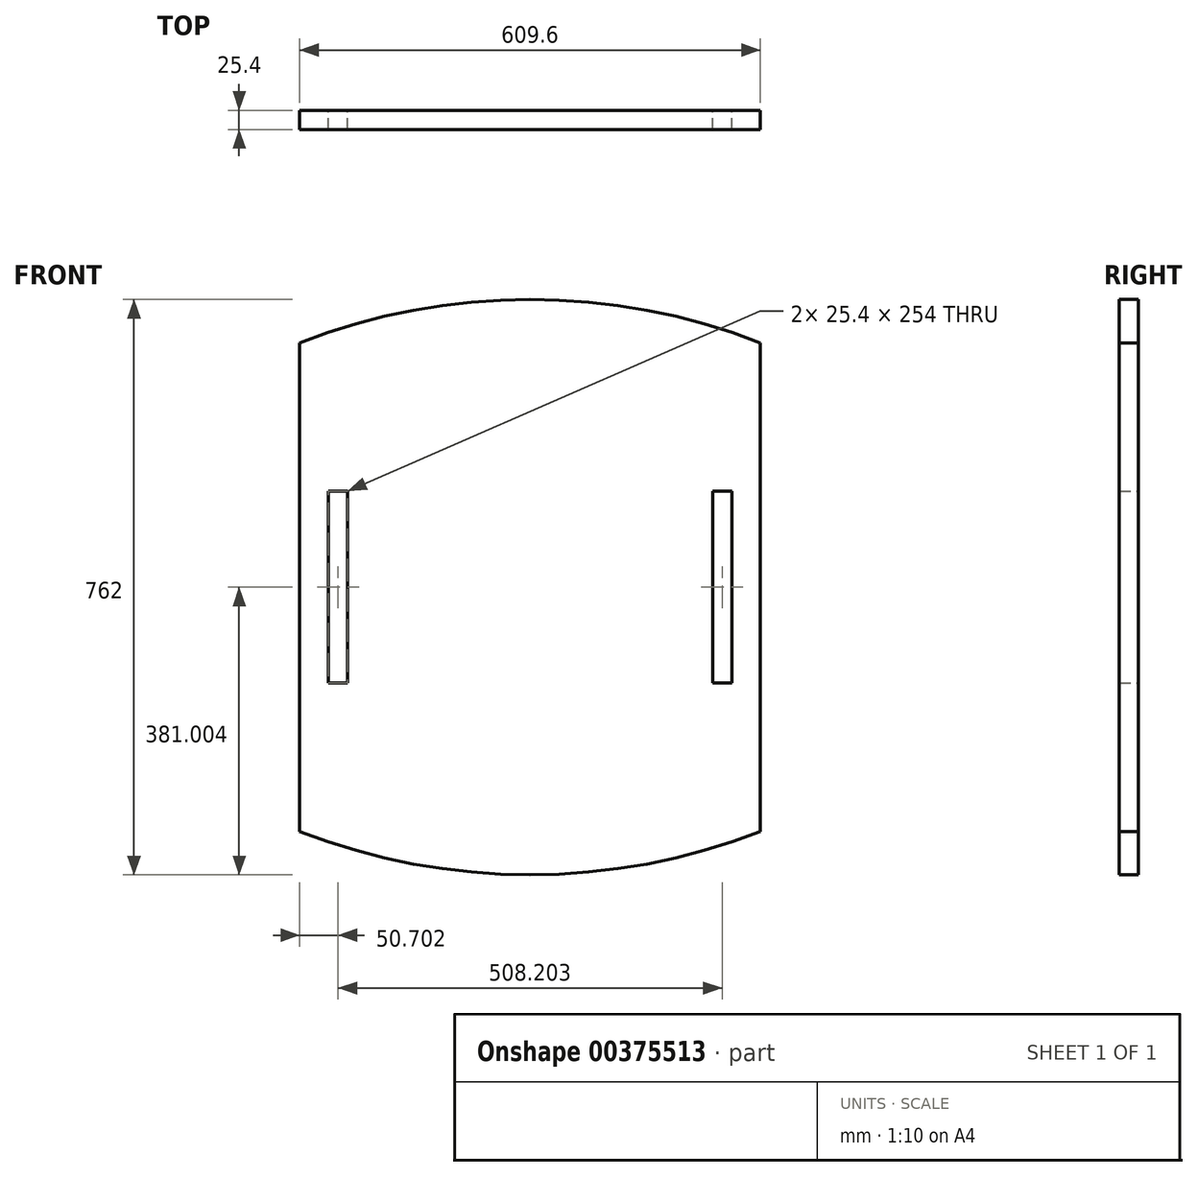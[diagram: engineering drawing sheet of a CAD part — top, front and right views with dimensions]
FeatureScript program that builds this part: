
annotation { "Feature Type Name" : "Feature", "Feature Type Description" : "" }
export const myFeature = defineFeature(function(context is Context, id is Id, definition is map)
    precondition{}
    {
        {
            var Q0;
            Q0=qCreatedBy(makeId("Front.planeOp"),FACE);
            var sketch = newSketch(context, id + "F0", { "sketchPlane" : qUnion([Q0])});
            skPoint(sketch, "E0.startSnap0", {"position": v(-108.45, 502.95) * mm});
            skArc(sketch, "E1", {"start": v(-412.87, -195.66) * mm, "mid": v(-108.07, -253.05) * mm, "end": v(196.73, -195.66) * mm});
            skArc(sketch, "E2.MirrorCS", {"start": v(-412.87, 451.57) * mm, "mid": v(-108.07, 508.95) * mm, "end": v(196.73, 451.57) * mm});
            skLineSegment(sketch, "E3", {"start": v(-412.87, 451.57) * mm, "end": v(-412.87, -195.66) * mm});
            skLineSegment(sketch, "E4", {"start": v(196.73, 451.57) * mm, "end": v(196.73, -195.66) * mm});
            skLineSegment(sketch, "E5.bottom", {"start": v(-349.47, 254.95) * mm, "end": v(-374.87, 254.95) * mm});
            skLineSegment(sketch, "E5.top", {"start": v(-349.47, 0.95) * mm, "end": v(-374.87, 0.95) * mm});
            skLineSegment(sketch, "E5.left", {"start": v(-349.47, 254.95) * mm, "end": v(-349.47, 0.95) * mm});
            skLineSegment(sketch, "E5.right", {"start": v(-374.87, 254.95) * mm, "end": v(-374.87, 0.95) * mm});
            skPoint(sketch, "E5.middle", {"position": v(-362.17, 127.95) * mm});
            skLineSegment(sketch, "E6.MirrorCS", {"start": v(133.34, 254.95) * mm, "end": v(133.34, 0.95) * mm});
            skLineSegment(sketch, "E7.MirrorCS", {"start": v(133.34, 254.95) * mm, "end": v(158.74, 254.95) * mm});
            skLineSegment(sketch, "E8.MirrorCS", {"start": v(158.74, 254.95) * mm, "end": v(158.74, 0.95) * mm});
            skLineSegment(sketch, "E9.MirrorCS", {"start": v(133.34, 0.95) * mm, "end": v(158.74, 0.95) * mm});
            skPoint(sketch, "E10", {"position": v(145.65, 126.8) * mm});
            skPoint(sketch, "E11.middle", {"position": v(-108.45, 126.8) * mm});
            skSolve(sketch);
        }
        {
            var Q0;
            Q0=makeQuery(id+"F0.imprint","IMPRINT",FACE,{"disambiguationData":[TD([[makeQuery(id+"F0.imprint","IMPRINT",EDGE,{"derivedFrom":sQuery(id+"F0.wireOp",EDGE,"E1")}),1.0]])]});
            extrude(context, id + "F1", {"entities" : qUnion([Q0]), "depth" : 25.4 * mm});
        }
    });
